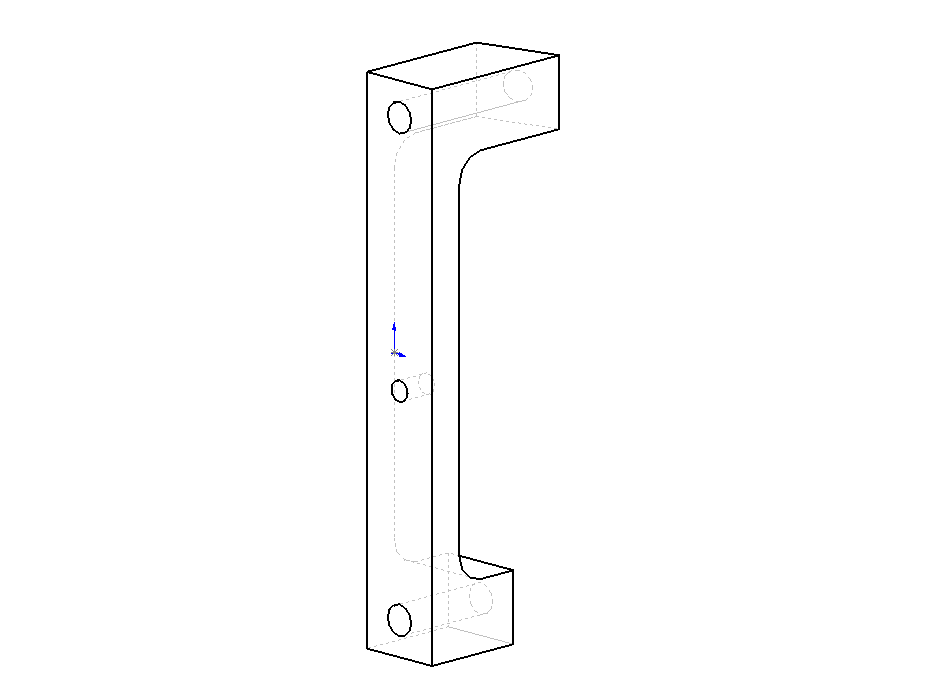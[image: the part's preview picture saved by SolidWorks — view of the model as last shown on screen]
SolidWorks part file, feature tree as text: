
SOLIDWORKS PART (.sldprt)
format: sldprt  version: not decoded by parser v0  size: 448,000 bytes
history: native  units: mm
features: sketch x7, extrude x3, cut_extrude x2, material x1, fillet x1, hole x1 + 1 further entry (+9 scaffold rows collapsed)
feature tree (25):
  scaffold x9  (default folders/planes/origin — collapsed)
  material  "Material <not specified>"
  "Origin"  ID=-1
  sketch  "Sketch1"  dims[D1=78.0mm D2=12.0mm D3=12.0mm D4=40.0mm]
  extrude  "Extrude1"  Depth=3mm
  sketch  "Sketch3"  dims[D1=2.9464mm D2=6.0mm D3=36.0mm]
  cut_extrude  "Cut-Extrude2"  [1 undecoded]
  sketch  "Sketch4"  dims[c1.D1=78.0mm c2.D1=90.0deg c3.D1=10.0mm c3.D2=10.0mm]
  extrude  "Extrude2"  Depth=12mm
  fillet  "Fillet1"  Radius=4mm
  sketch  "Sketch5"  dims[c1.D1=~12.465808mm c2.D1=15.0deg c3.D1=12.0mm c4.D1=15.0deg c5.D1=~12.833406mm c6.D1=15.2deg c6.D2=3.808mm]
  cut_extrude  "Cut-Extrude3"  [1 undecoded]
  sketch  "Sketch6"  dims[c1.D1=5.1824mm c1.D2=~14.62962mm c2.D2=15.3deg]
  extrude  "Extrude3"  [1 undecoded]
  hole  "#8 Clearance Hole1"  Diameter=4.3053mm Depth=15mm
  sketch  "3DSketch1"  dims[c1.D1=~68.343373mm c1.D4=67.5mm c1.D2=6.0mm c1.D3=5.0mm c2.D1=5.0mm]
  sketch  "Sketch7"  dims[hole-wizard template sketch: 60 standard entries collapsed; hole parameters kept: c18.Thru Hole Depth=15.0mm]
decode coverage: 11 of 14 modeling features carry decoded parameters; 1 rows unclassified (native names shown)
note: ~ marks probable driven/reference dimensions
note: 3 parameter values undecoded
summary: no parameter record found for 3 features
note: suppression state not decoded; provenance and decode notes live in map.json
